AUTODESK INVENTOR PART (.ipt)
format: ipt  version: 2015 SP1 (Build 190203100, 203)  size: 179,200 bytes
history: native  units: in
note: dims shown in document units (in); Inventor stores cm internally (conversion verified against a paired STEP export)
features: sketch x2, plane x1, hole x1
ambient origin geometry x8: Origin, YZ Plane, XZ Plane, XY Plane, X Axis, Y Axis, Z Axis, Center Point
bodies: Body1 (feature_tree)
feature tree (4):
  plane  "Work Plane1"
  sketch  "Sketch2"  dims[d0=16.5in d21=0.25in d22=0.0in]
  hole  "Hole1"  [1 undecoded]
  sketch  "Sketch3"  dims[d23=0.125in d27=1.5in d31=0.163in d32=0.75in d33=0.119in d34=0.25in d35=0.5635in d36=1.0in d37=0.8108in]
note: 1 required parameter value undecoded (feature->parameter linkage not recoverable at this tier; creation-order binding heuristic only, values carry confidence <= 0.55)
